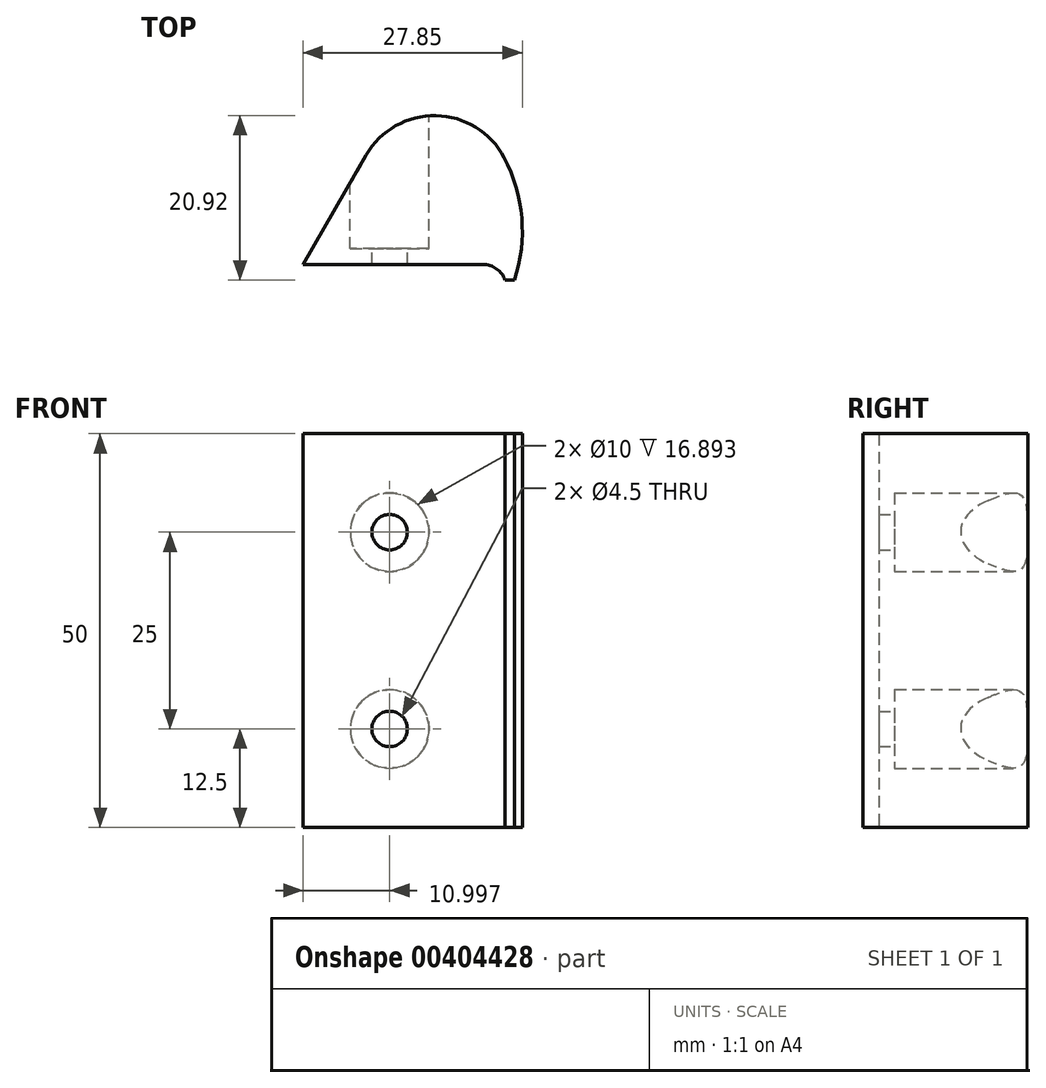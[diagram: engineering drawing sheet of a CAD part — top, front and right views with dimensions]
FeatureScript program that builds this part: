
annotation { "Feature Type Name" : "Feature", "Feature Type Description" : "" }
export const myFeature = defineFeature(function(context is Context, id is Id, definition is map)
    precondition{}
    {
        {
            var Q0;
            Q0=qCreatedBy(makeId("Top.planeOp"),FACE);
            var sketch = newSketch(context, id + "F0", { "sketchPlane" : qUnion([Q0])});
            skCircle(sketch, "E0", {"center": v(0, 0) * mm, "radius": 70 * mm, "construction": true});
            skLineSegment(sketch, "E1", {"start": v(-74.47, -73) * mm, "end": v(62, -73) * mm, "construction": true});
            skLineSegment(sketch, "E2", {"start": v(65, -76) * mm, "end": v(65, -139.02) * mm, "construction": true});
            skLineSegment(sketch, "E3", {"start": v(-9.02, 63.72) * mm, "end": v(77.99, -81.58) * mm, "construction": true});
            skLineSegment(sketch, "E4", {"start": v(67, -42.16) * mm, "end": v(67, -107) * mm, "construction": true});
            skCircle(sketch, "E5", {"center": v(0, 0) * mm, "radius": 75 * mm, "construction": true});
            skArc(sketch, "E6", {"start": v(64.68, -59.41) * mm, "mid": v(56.03, -54.09) * mm, "end": v(47.18, -59.08) * mm});
            skLineSegment(sketch, "E7", {"start": v(47.18, -59.08) * mm, "end": v(39.15, -73) * mm});
            skLineSegment(sketch, "E8", {"start": v(39.15, -73) * mm, "end": v(62, -73) * mm});
            skPoint(sketch, "E9.visualSharp", {"position": v(66, -75) * mm});
            skArc(sketch, "E9.filletArc", {"start": v(65, -76) * mm, "mid": v(64.12, -73.88) * mm, "end": v(62, -73) * mm, "construction": true});
            skArc(sketch, "E10", {"start": v(64.83, -75) * mm, "mid": v(63.73, -73.55) * mm, "end": v(62, -73) * mm});
            skLineSegment(sketch, "E11", {"start": v(64.83, -75) * mm, "end": v(66, -75) * mm});
            skArc(sketch, "E12", {"start": v(66, -75) * mm, "mid": v(66.93, -67.07) * mm, "end": v(64.68, -59.41) * mm});
            skSolve(sketch);
        }
        {
            var Q0;
            Q0=qSketchRegion(id+"F0",true);
            extrude(context, id + "F1", {"entities" : qUnion([Q0]), "depth" : 50 * mm});
        }
        {
            var Q0;
            Q0=qCreatedBy(makeId("Front.planeOp"),FACE);
            var sketch = newSketch(context, id + "F2", { "sketchPlane" : qUnion([Q0])});
            skPoint(sketch, "E13", {"position": v(50.15, 37.5) * mm});
            skPoint(sketch, "E14", {"position": v(50.15, 12.5) * mm});
            skLineSegment(sketch, "E15", {"start": v(50.15, 37.5) * mm, "end": v(50.15, 12.5) * mm, "construction": true});
            skSolve(sketch);
        }
        {
            var Q0;
            Q0=sQuery(id+"F2.wireOp",VERTEX,"E13");
            var Q1;
            Q1=makeQuery(id+"F1.opExtrude","SWEPT_BODY",BODY,{"disambiguationData":[OSD([sQuery(id+"F0.wireOp",EDGE,"TtpqnqnA-3x2I-fmXF-Hiot-M3ifufQSjGu8"),sQuery(id+"F0.wireOp",EDGE,"E6"),sQuery(id+"F0.wireOp",EDGE,"E7"),sQuery(id+"F0.wireOp",EDGE,"E8"),sQuery(id+"F0.wireOp",EDGE,"E10"),sQuery(id+"F0.wireOp",EDGE,"E11")])]});
            hole(context, id + "F3", {"style" : HoleStyle.C_BORE, "endStyle" : HoleEndStyle.THROUGH, "oppositeDirection" : true, "holeDiameter" : 4.5 * mm, "cBoreDiameter" : 10 * mm, "cBoreDepth" : 71 * mm, "isTappedThrough" : true, "tappedDepth" : 12 * mm, "tapClearance" : 3, "startFromSketch" : true, "locations" : qUnion([Q0]), "scope" : qUnion([Q1])});
        }
        {
            var Q0;
            Q0=sQuery(id+"F2.wireOp",VERTEX,"E14");
            var Q1;
            Q1=makeQuery(id+"F1.opExtrude","SWEPT_BODY",BODY,{"disambiguationData":[OSD([sQuery(id+"F0.wireOp",EDGE,"TtpqnqnA-3x2I-fmXF-Hiot-M3ifufQSjGu8"),sQuery(id+"F0.wireOp",EDGE,"E6"),sQuery(id+"F0.wireOp",EDGE,"E7"),sQuery(id+"F0.wireOp",EDGE,"E8"),sQuery(id+"F0.wireOp",EDGE,"E10"),sQuery(id+"F0.wireOp",EDGE,"E11")])]});
            hole(context, id + "F4", {"style" : HoleStyle.C_BORE, "endStyle" : HoleEndStyle.THROUGH, "oppositeDirection" : true, "holeDiameter" : 4.5 * mm, "cBoreDiameter" : 10 * mm, "cBoreDepth" : 71 * mm, "isTappedThrough" : true, "tappedDepth" : 12 * mm, "tapClearance" : 3, "startFromSketch" : true, "locations" : qUnion([Q0]), "scope" : qUnion([Q1])});
        }
    });
